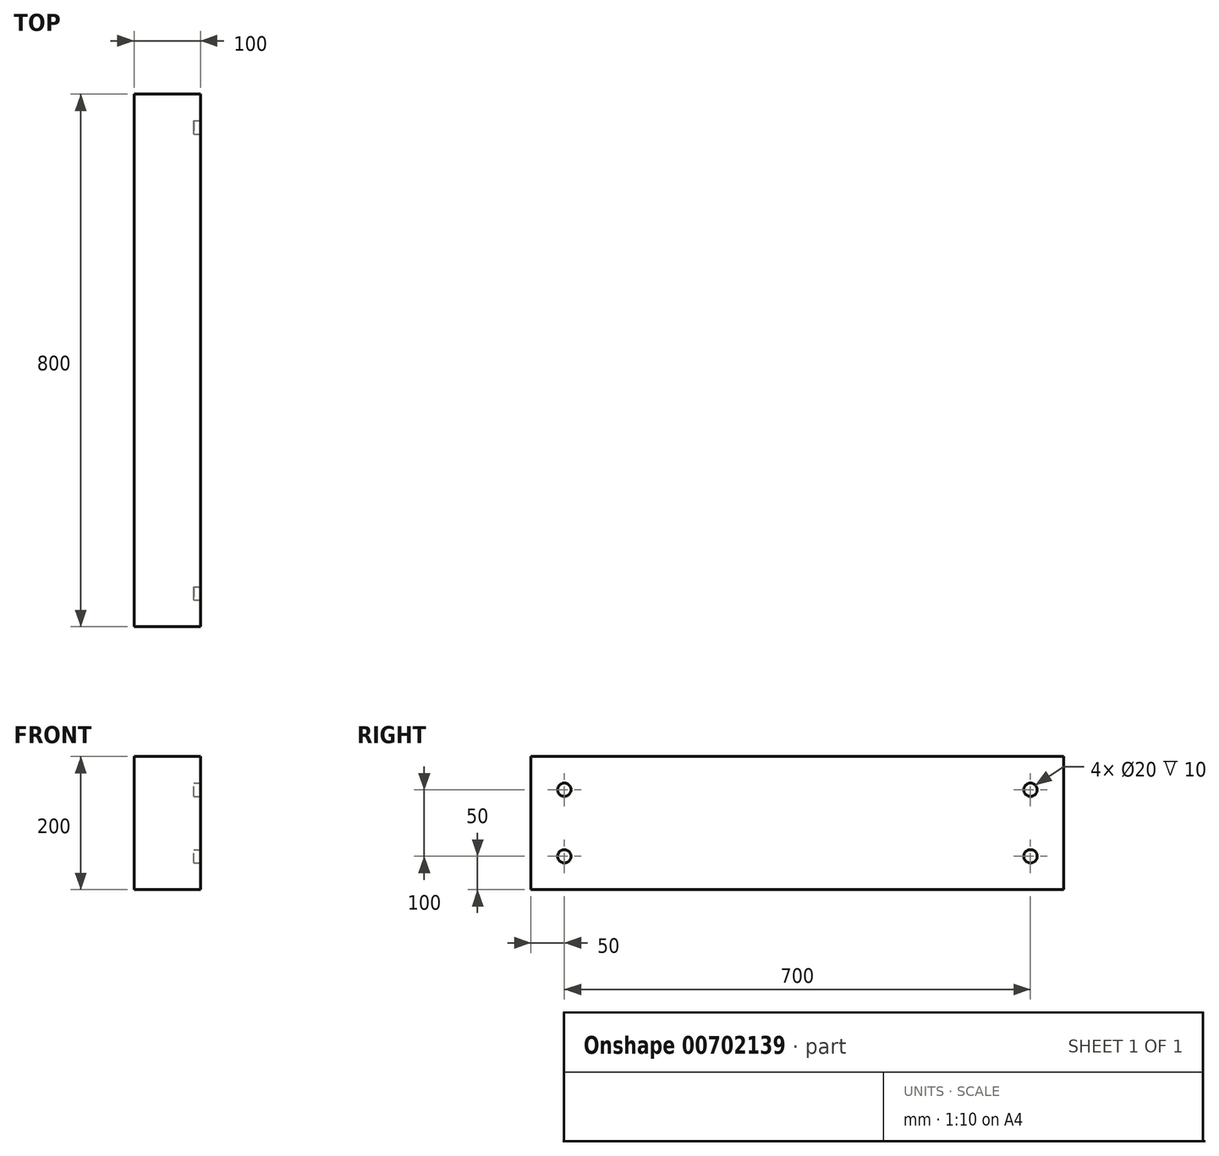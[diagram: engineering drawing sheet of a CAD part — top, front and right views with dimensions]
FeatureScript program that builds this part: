
annotation { "Feature Type Name" : "Feature", "Feature Type Description" : "" }
export const myFeature = defineFeature(function(context is Context, id is Id, definition is map)
    precondition{}
    {
        {
            var Q0;
            Q0=qCreatedBy(makeId("Front.planeOp"),FACE);
            var sketch = newSketch(context, id + "F0", { "sketchPlane" : qUnion([Q0])});
            skLineSegment(sketch, "E0.bottom", {"start": v(0, 0) * mm, "end": v(-100, 0) * mm});
            skLineSegment(sketch, "E0.top", {"start": v(0, 200) * mm, "end": v(-100, 200) * mm});
            skLineSegment(sketch, "E0.left", {"start": v(0, 0) * mm, "end": v(0, 200) * mm});
            skLineSegment(sketch, "E0.right", {"start": v(-100, 0) * mm, "end": v(-100, 200) * mm});
            skSolve(sketch);
        }
        {
            var Q0;
            Q0=qSketchRegion(id+"F0",true);
            extrude(context, id + "F1", {"entities" : qUnion([Q0]), "depth" : 800 * mm, "offsetDistance" : 25 * mm});
        }
        {
            var Q0;
            Q0=makeQuery(id+"F1.opExtrude","SWEPT_FACE",FACE,{"disambiguationData":[OSD([sQuery(id+"F0.wireOp",EDGE,"E0.left")])]});
            var sketch = newSketch(context, id + "F2", { "sketchPlane" : qUnion([Q0])});
            skCircle(sketch, "E1", {"center": v(-750, 150) * mm, "radius": 10 * mm});
            skCircle(sketch, "E2", {"center": v(-750, 50) * mm, "radius": 10 * mm});
            skCircle(sketch, "E3", {"center": v(-50, 150) * mm, "radius": 10 * mm});
            skCircle(sketch, "E4", {"center": v(-50, 50) * mm, "radius": 10 * mm});
            skSolve(sketch);
        }
        {
            var Q0;
            Q0 = qSketchRegion(id + "F2", true);
            extrude(context, id + "F3", {"entities" : qUnion([Q0]), "operationType" : NewBodyOperationType.REMOVE, "oppositeDirection" : true, "depth" : 10 * mm, "offsetDistance" : 25 * mm});
        }
    });
